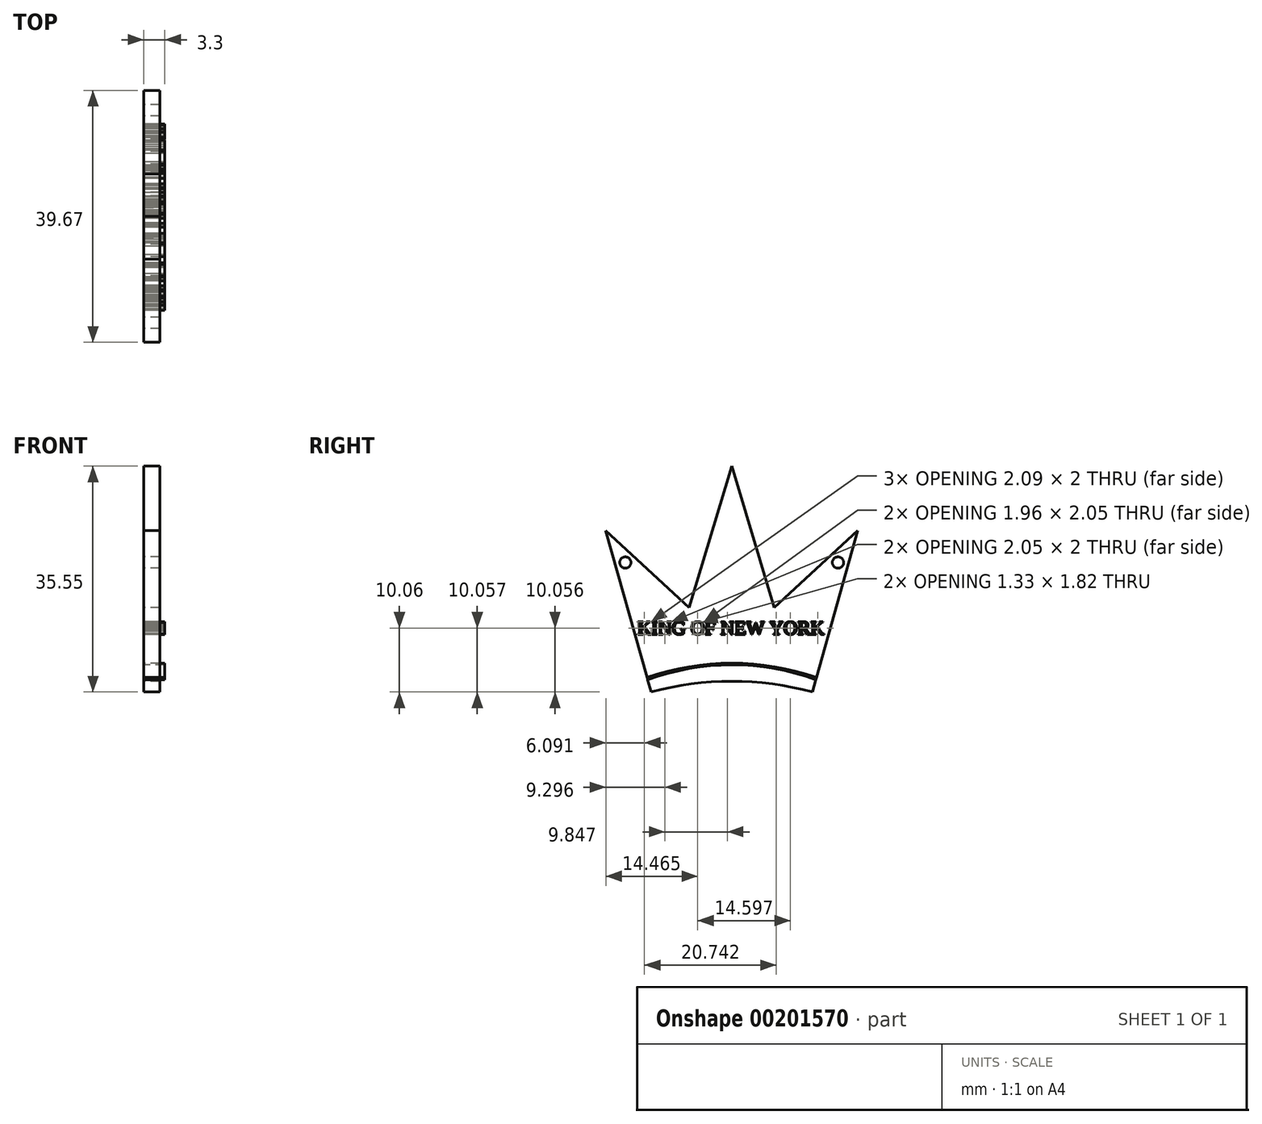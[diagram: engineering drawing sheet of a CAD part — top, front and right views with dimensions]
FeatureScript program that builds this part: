
annotation { "Feature Type Name" : "Feature", "Feature Type Description" : "" }
export const myFeature = defineFeature(function(context is Context, id is Id, definition is map)
    precondition{}
    {
        {
            var Q0;
            Q0=qCreatedBy(makeId("Right.planeOp"),FACE);
            var sketch = newSketch(context, id + "F0", { "sketchPlane" : qUnion([Q0])});
            skLineSegment(sketch, "E0", {"start": v(-59.22, 116.86) * mm, "end": v(-52.08, 91.46) * mm});
            skArc(sketch, "E1", {"start": v(-26.68, 91.46) * mm, "mid": v(-39.38, 93.14) * mm, "end": v(-52.08, 91.46) * mm});
            skLineSegment(sketch, "E2", {"start": v(-59.22, 116.86) * mm, "end": v(-46.1, 104.77) * mm});
            skLineSegment(sketch, "E3", {"start": v(-46.1, 104.77) * mm, "end": v(-39.4, 127.01) * mm});
            skLineSegment(sketch, "E4", {"start": v(-39.4, 127.01) * mm, "end": v(-32.71, 104.73) * mm});
            skLineSegment(sketch, "E5", {"start": v(-58.57, 116.26) * mm, "end": v(-59.22, 116.86) * mm});
            skLineSegment(sketch, "E6.MirrorCS", {"start": v(-19.55, 116.84) * mm, "end": v(-32.71, 104.73) * mm});
            skLineSegment(sketch, "E7.MirrorCS", {"start": v(-19.55, 116.84) * mm, "end": v(-26.68, 91.46) * mm});
            skArc(sketch, "E8", {"start": v(-26.04, 93.74) * mm, "mid": v(-39.38, 96) * mm, "end": v(-52.73, 93.74) * mm});
            skArc(sketch, "E9", {"start": v(-26.15, 93.38) * mm, "mid": v(-39.38, 95.73) * mm, "end": v(-52.62, 93.36) * mm});
            skText(sketch, "E10", { "text": "KING OF NEW YORK", "fontName": "Tinos-Regular.ttf"});
            skCircle(sketch, "E11.MirrorC", {"center": v(-56.15, 111.84) * mm, "radius": 0.89 * mm});
            skLineSegment(sketch, "E12", {"start": v(-39.4, 127.01) * mm, "end": v(-39.4, 119.82) * mm, "construction": true});
            skCircle(sketch, "E13.MirrorC", {"center": v(-22.67, 111.84) * mm, "radius": 0.89 * mm});
            const initialGuessF0  = {"E10": [-0.05426, 0.10052, 1, 0, 0.0022]};
            skSetInitialGuess(sketch, initialGuessF0);
            skSolve(sketch);
        }
        {
            var Q0;
            {var subQ0=sQuery(id+"F0.wireOp",EDGE,"E0");Q0=makeQuery(id+"F0.imprint","IMPRINT",FACE,{"disambiguationData":[TD([[makeQuery(id+"F0.imprint","IMPRINT",EDGE,{"derivedFrom":subQ0}),1.0]])]});}
            var Q1;
            Q1=makeQuery(id+"F0.imprint","IMPRINT",FACE,{"disambiguationData":[TD([[makeQuery(id+"F0.imprint","IMPRINT",EDGE,{"derivedFrom":sQuery(id+"F0.wireOp",EDGE,"GQQ1rd4y-LrSX-NBck-YKuN-i1aV1AsWi9N3")}),1.0]])]});
            var Q2;
            Q2=makeQuery(id+"F0.imprint","IMPRINT",FACE,{"disambiguationData":[TD([[makeQuery(id+"F0.imprint","IMPRINT",EDGE,{"derivedFrom":sQuery(id+"F0.wireOp",EDGE,"1a751295-b812-4111-9483-698d7f5b56d20.MirrorC")}),1.0]])]});
            var Q3;
            Q3=makeQuery(id+"F0.imprint","IMPRINT",FACE,{"disambiguationData":[TD([[makeQuery(id+"F0.imprint","IMPRINT",EDGE,{"derivedFrom":sQuery(id+"F0.wireOp",EDGE,"cca22276-4f91-4f59-8e96-016f3934cc280.MirrorC")}),-1.0]])]});
            var Q4;
            Q4=makeQuery(id+"F0.imprint","IMPRINT",FACE,{"disambiguationData":[TD([[makeQuery(id+"F0.imprint","IMPRINT",EDGE,{"derivedFrom":sQuery(id+"F0.wireOp",EDGE,"a90a5097-b338-402b-a556-6614c61f2fdb.sketch_text.stroke-83")}),1.0]])]});
            var Q5;
            Q5=makeQuery(id+"F0.imprint","IMPRINT",FACE,{"disambiguationData":[TD([[makeQuery(id+"F0.imprint","IMPRINT",EDGE,{"derivedFrom":sQuery(id+"F0.wireOp",EDGE,"a90a5097-b338-402b-a556-6614c61f2fdb.sketch_text.stroke-209")}),1.0]])]});
            var Q6;
            Q6=makeQuery(id+"F0.imprint","IMPRINT",FACE,{"disambiguationData":[TD([[makeQuery(id+"F0.imprint","IMPRINT",EDGE,{"derivedFrom":sQuery(id+"F0.wireOp",EDGE,"a90a5097-b338-402b-a556-6614c61f2fdb.sketch_text.stroke-244")}),1.0]])]});
            var Q7;
            Q7=makeQuery(id+"F0.imprint","IMPRINT",FACE,{"disambiguationData":[TD([[makeQuery(id+"F0.imprint","IMPRINT",EDGE,{"derivedFrom":sQuery(id+"F0.wireOp",EDGE,"E2")}),-1.0]])]});
            var Q8;
            Q8=makeQuery(id+"F0.imprint","IMPRINT",FACE,{"disambiguationData":[TD([[makeQuery(id+"F0.imprint","IMPRINT",EDGE,{"derivedFrom":sQuery(id+"F0.wireOp",EDGE,"a084564a-4ab7-4054-93ee-e372b2ba83890.MirrorC")}),1.0]])]});
            var Q9;
            {var subQ0=sQuery(id+"F0.wireOp",EDGE,"E1");Q9=makeQuery(id+"F0.imprint","IMPRINT",FACE,{"disambiguationData":[TD([[makeQuery(id+"F0.imprint","IMPRINT",EDGE,{"derivedFrom":subQ0}),-1.0]])]});}
            var Q10;
            Q10=makeQuery(id+"F0.imprint","IMPRINT",FACE,{"disambiguationData":[TD([[makeQuery(id+"F0.imprint","IMPRINT",EDGE,{"derivedFrom":sQuery(id+"F0.wireOp",EDGE,"E11.MirrorC")}),-1.0]])]});
            var Q11;
            Q11=makeQuery(id+"F0.imprint","IMPRINT",FACE,{"disambiguationData":[TD([[makeQuery(id+"F0.imprint","IMPRINT",EDGE,{"derivedFrom":sQuery(id+"F0.wireOp",EDGE,"E10.sketch_text.stroke-83")}),1.0]])]});
            var Q12;
            Q12=makeQuery(id+"F0.imprint","IMPRINT",FACE,{"disambiguationData":[TD([[makeQuery(id+"F0.imprint","IMPRINT",EDGE,{"derivedFrom":sQuery(id+"F0.wireOp",EDGE,"E10.sketch_text.stroke-209")}),1.0]])]});
            var Q13;
            Q13=makeQuery(id+"F0.imprint","IMPRINT",FACE,{"disambiguationData":[TD([[makeQuery(id+"F0.imprint","IMPRINT",EDGE,{"derivedFrom":sQuery(id+"F0.wireOp",EDGE,"E10.sketch_text.stroke-244")}),1.0]])]});
            extrude(context, id + "F1", {"entities" : qUnion([Q0, Q1, Q2, Q3, Q4, Q5, Q6, Q7, Q8, Q9, Q10, Q11, Q12, Q13]), "depth" : 2.54 * mm});
        }
        {
            var Q0;
            Q0=makeQuery(id+"F0.imprint","IMPRINT",FACE,{"disambiguationData":[TD([[makeQuery(id+"F0.imprint","IMPRINT",EDGE,{"derivedFrom":sQuery(id+"F0.wireOp",EDGE,"E10.sketch_text.stroke-0")}),-1.0]])]});
            var Q1;
            Q1=makeQuery(id+"F0.imprint","IMPRINT",FACE,{"disambiguationData":[TD([[makeQuery(id+"F0.imprint","IMPRINT",EDGE,{"derivedFrom":sQuery(id+"F0.wireOp",EDGE,"E10.sketch_text.stroke-26")}),-1.0]])]});
            var Q2;
            Q2=makeQuery(id+"F0.imprint","IMPRINT",FACE,{"disambiguationData":[TD([[makeQuery(id+"F0.imprint","IMPRINT",EDGE,{"derivedFrom":sQuery(id+"F0.wireOp",EDGE,"E10.sketch_text.stroke-38")}),-1.0]])]});
            var Q3;
            Q3=makeQuery(id+"F0.imprint","IMPRINT",FACE,{"disambiguationData":[TD([[makeQuery(id+"F0.imprint","IMPRINT",EDGE,{"derivedFrom":sQuery(id+"F0.wireOp",EDGE,"E10.sketch_text.stroke-83")}),-1.0]])]});
            var Q4;
            Q4=makeQuery(id+"F0.imprint","IMPRINT",FACE,{"disambiguationData":[TD([[makeQuery(id+"F0.imprint","IMPRINT",EDGE,{"derivedFrom":sQuery(id+"F0.wireOp",EDGE,"E10.sketch_text.stroke-98")}),-1.0]])]});
            var Q5;
            Q5=makeQuery(id+"F0.imprint","IMPRINT",FACE,{"disambiguationData":[TD([[makeQuery(id+"F0.imprint","IMPRINT",EDGE,{"derivedFrom":sQuery(id+"F0.wireOp",EDGE,"E10.sketch_text.stroke-121")}),-1.0]])]});
            var Q6;
            Q6=makeQuery(id+"F0.imprint","IMPRINT",FACE,{"disambiguationData":[TD([[makeQuery(id+"F0.imprint","IMPRINT",EDGE,{"derivedFrom":sQuery(id+"F0.wireOp",EDGE,"E10.sketch_text.stroke-58")}),-1.0]])]});
            var Q7;
            Q7=makeQuery(id+"F0.imprint","IMPRINT",FACE,{"disambiguationData":[TD([[makeQuery(id+"F0.imprint","IMPRINT",EDGE,{"derivedFrom":sQuery(id+"F0.wireOp",EDGE,"E10.sketch_text.stroke-209")}),-1.0]])]});
            var Q8;
            Q8=makeQuery(id+"F0.imprint","IMPRINT",FACE,{"disambiguationData":[TD([[makeQuery(id+"F0.imprint","IMPRINT",EDGE,{"derivedFrom":sQuery(id+"F0.wireOp",EDGE,"E10.sketch_text.stroke-224")}),-1.0]])]});
            var Q9;
            Q9=makeQuery(id+"F0.imprint","IMPRINT",FACE,{"disambiguationData":[TD([[makeQuery(id+"F0.imprint","IMPRINT",EDGE,{"derivedFrom":sQuery(id+"F0.wireOp",EDGE,"E10.sketch_text.stroke-188")}),-1.0]])]});
            var Q10;
            Q10=makeQuery(id+"F0.imprint","IMPRINT",FACE,{"disambiguationData":[TD([[makeQuery(id+"F0.imprint","IMPRINT",EDGE,{"derivedFrom":sQuery(id+"F0.wireOp",EDGE,"E10.sketch_text.stroke-251")}),-1.0]])]});
            var Q11;
            Q11=makeQuery(id+"F0.imprint","IMPRINT",FACE,{"disambiguationData":[TD([[makeQuery(id+"F0.imprint","IMPRINT",EDGE,{"derivedFrom":sQuery(id+"F0.wireOp",EDGE,"E10.sketch_text.stroke-141")}),-1.0]])]});
            var Q12;
            Q12=makeQuery(id+"F0.imprint","IMPRINT",FACE,{"disambiguationData":[TD([[makeQuery(id+"F0.imprint","IMPRINT",EDGE,{"derivedFrom":sQuery(id+"F0.wireOp",EDGE,"E10.sketch_text.stroke-167")}),-1.0]])]});
            var Q13;
            {var subQ0=sQuery(id+"F0.wireOp",EDGE,"E8");Q13=makeQuery(id+"F0.imprint","IMPRINT",FACE,{"disambiguationData":[TD([[makeQuery(id+"F0.imprint","IMPRINT",EDGE,{"derivedFrom":subQ0}),1.0]])]});}
            extrude(context, id + "F2", {"entities" : qUnion([Q0, Q1, Q2, Q3, Q4, Q5, Q6, Q7, Q8, Q9, Q10, Q11, Q12, Q13]), "depth" : 3.3 * mm});
        }
    });
